# Revit family: Water_Heater-Rinnai-TRS02ILi-Freestanding-Rack_System
name_source: partatom
category: Mechanical Equipment
revit_build: Autodesk Revit MEP 2012 (Build: 20110916_2132(x64)
units: mm (PartAtom-declared; Revit-internal decimal feet)

## types (1)
- TRS02ILi
    Air Supply Connector = Air Supply Connection
    Applicable Altitude Range = 0-10,200ft (0-3,109m)
    Assembly Code = D3010500
    Clearance for Back = 0"
    Clearance for Front = 0"
    Clearance for Ground or Bottom = 0"
    Clearance for Sides = 0"
    Clearance for Top = 0"
    Cold Water Branch Connector = Cold Water Branch Connection
    Cold Water Connector = Cold Water Connection Inlet
    Cold Water Inlet Radius = 1 1/4"
    Cold Water Trunk Connector = Cold Water Trunk Connectoion
    Combustibles = No
    Combustion Air = Indoor or outdoor
    Default Elevation = 48"
    Depth = 29"
    Description = Condensing Tankless Water Heater
    Door = Metal - Rinnai - Aluminum - Polished Sliver
    Dry Weight = 576.00 lb
    Electrical Consumption Range = Normal: 64 w, Standby: 2 w
    Exhaust Vent Length Note = 100 ft
    First Hour Rating = 0.00 GPM
    Flow Rate at 100 Deg F Rise = 15.20 GPM
    Flow Rate at 70 Deg F Rise = 21.60 GPM
    Frame Finish = Metal - Rinnai - Anodized Aluminum
    Frequency = 60 Hz
    Gas Branch Connector = Gas Branch Connection
    Gas Branch Line Diameter = 3/4"
    Gas Branch Line Radius = 3/8"
    Gas Connection = Gas Connection
    Gas Input Range = 15,200 - 796,000 BTU/h
    Gas Input Rate = 796.0 Btu/h
    Gas Manifold Pressure High Fire = 0"
    Gas Manifold Pressure Low Fire = 0"
    Gas Supply Pressure Max = 13 1/2"
    Gas Supply Pressure Min = 8"
    Gas Supply Radius = 1"
    Gas Trunk Connector = Gas Trunk Connectoion
    Gas Trunk Line Finish = Metal - Rinnai - Aluminum - Polished Sliver
    Hardware = Metal - Rinnai - Aluminum Frame - Painted White
    Height = 58"
    Hot And Cold Water Trunk Line = Metal - Rinnai - Bronze
    Hot Water Branch Connector = Hot Water Branch Connection
    Hot Water Connector = Hot Water Connection Outlet
    Hot Water Outlet Radius = 1 1/4"
    Hot Water Trunk Connector = Hot Water Trunk Connectoion
    Input Rate Maximum = 796000.0 Btu/h
    Installation Location = Indoor and outdoor
    Liquid Propane = Yes
    Manufacturer = Rinnai America Corporation
    Manufacturer Fax = 678-829-1666
    Max Amperage = 16 A
    Model = TRS02ILi
    Natural Gas = No
    Panel = Metal - Rinnai - Aluminum Frame - Painted White
    Recovery for 100 Deg Rise = 987-1197 gal/h
    Revit Object Download Link = http://library.smartbim.com
    Storage Tank Volume = 100.40 GPM
    Subcategory = Tankless Water Heaters
    Thermal Efficiency Rating = 0.96
    URL = http://www.rinnai.us
    Unit = Metal - Rinnai - Aluminum Frame - Painted White
    Vent Connector = Vent Connection
    Venting = Rinnai Common Vent System
    Voltage = 120 V
    Warranty = Commercial: 6-year on heat exchanger, 5-year on parts, up to 2 years labor
    Wattage = 64 W
    Width = 44"

## geometry (parser evidence)
native form markers: Blend x8, Sweep x16
no freeform markers — native parametric forms only
